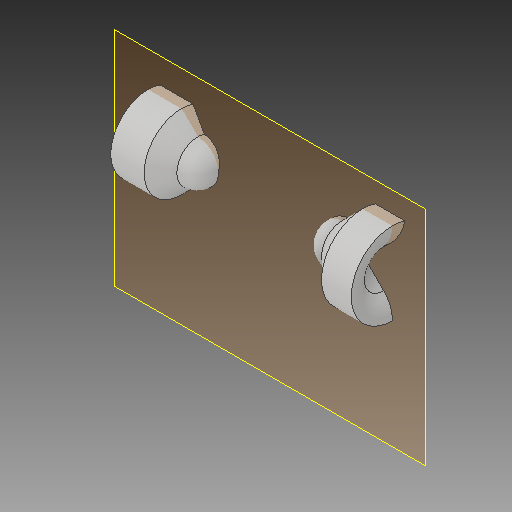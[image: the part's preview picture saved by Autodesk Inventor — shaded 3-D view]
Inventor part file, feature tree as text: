
AUTODESK INVENTOR PART (.ipt)
format: ipt  version: 2019.3 (Build 233278000, 278)  size: 161,792 bytes
history: native  units: mm
features: reference x5, other x3, plane x1, revolve x1, sketch x1
ambient origin geometry x8: Origin, YZ Plane, XZ Plane, XY Plane, X Axis, Y Axis, Z Axis, Center Point
bodies: Body1 (feature_tree)
feature tree (11):
  plane  "Work Plane1"
  revolve  "Revolution3"  [1 undecoded]
  sketch  "Sketch1"  dims[d5=90.0deg d6=34.557519mm]
  reference  "Reference1"
  reference  "Reference2"
  reference  "Reference3"
  reference  "Reference4"
  reference  "Reference5"
  parser-record x1  (decoder bookkeeping rows leaked as tree rows — omitted from the tree; the rows remain in map.json)
  other  "mount assem.iam"
  other  "mounter:1"
note: 1 file-system path scrubbed to <path> (originals preserved in map.json)
note: 1 required parameter value undecoded (feature->parameter linkage not recoverable at this tier; creation-order binding heuristic only, values carry confidence <= 0.55)
